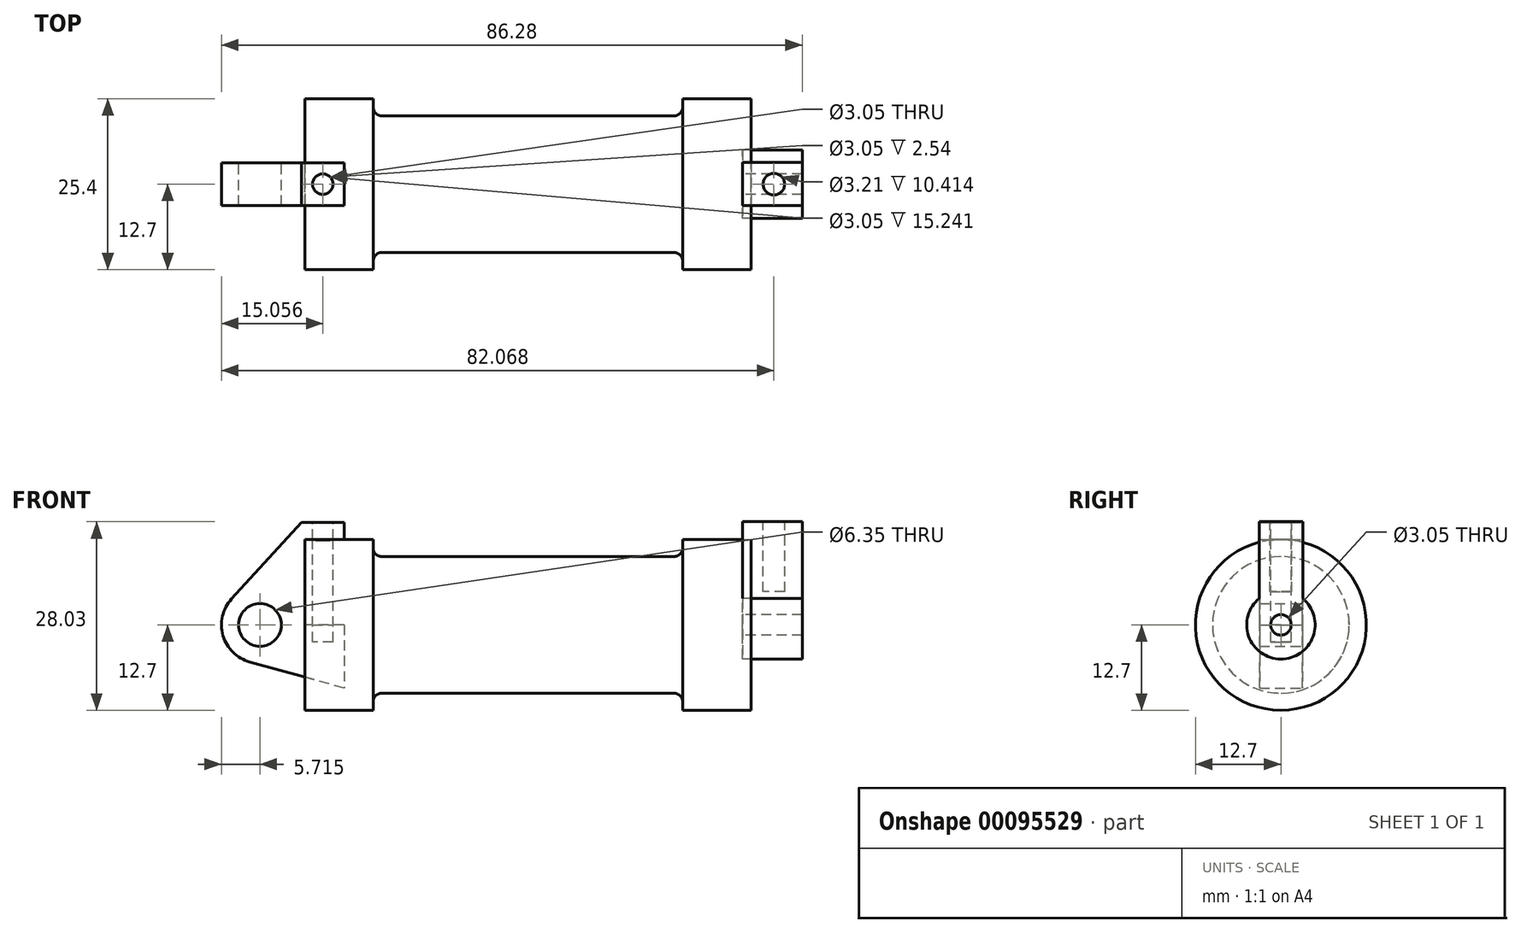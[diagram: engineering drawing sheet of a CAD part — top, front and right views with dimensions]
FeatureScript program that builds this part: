
annotation { "Feature Type Name" : "Feature", "Feature Type Description" : "" }
export const myFeature = defineFeature(function(context is Context, id is Id, definition is map)
    precondition{}
    {
        {
            var Q0;
            Q0=qCreatedBy(makeId("Front.planeOp"),FACE);
            var sketch = newSketch(context, id + "F0", { "sketchPlane" : qUnion([Q0])});
            skLineSegment(sketch, "E0", {"start": v(0, 0) * mm, "end": v(0, 12.7) * mm});
            skLineSegment(sketch, "E1", {"start": v(0, 12.7) * mm, "end": v(10.16, 12.7) * mm});
            skLineSegment(sketch, "E2", {"start": v(10.16, 12.7) * mm, "end": v(10.16, 10.16) * mm});
            skLineSegment(sketch, "E3", {"start": v(10.16, 10.16) * mm, "end": v(56.13, 10.16) * mm});
            skLineSegment(sketch, "E4", {"start": v(56.13, 10.16) * mm, "end": v(56.13, 12.7) * mm});
            skLineSegment(sketch, "E5", {"start": v(56.13, 12.7) * mm, "end": v(66.3, 12.7) * mm});
            skLineSegment(sketch, "E6", {"start": v(66.3, 12.7) * mm, "end": v(66.3, 0) * mm});
            skLineSegment(sketch, "E7", {"start": v(66.3, 0) * mm, "end": v(0, 0) * mm});
            skLineSegment(sketch, "E8", {"start": v(5.84, 15.24) * mm, "end": v(-0.5, 15.24) * mm});
            skLineSegment(sketch, "E9", {"start": v(-0.5, 15.24) * mm, "end": v(-10.88, 3.85) * mm});
            skLineSegment(sketch, "E10", {"start": v(0, 0) * mm, "end": v(-6.65, 0) * mm});
            skCircle(sketch, "E11", {"center": v(-6.65, 0) * mm, "radius": 5.72 * mm});
            skCircle(sketch, "E12", {"center": v(-6.65, 0) * mm, "radius": 3.18 * mm});
            skLineSegment(sketch, "E13", {"start": v(5.84, 15.24) * mm, "end": v(5.84, -9.4) * mm});
            skLineSegment(sketch, "E14", {"start": v(5.84, -9.4) * mm, "end": v(-8.18, -5.5) * mm});
            skSolve(sketch);
        }
        {
            var Q0;
            {var subQ0=sQuery(id+"F0.wireOp",EDGE,"E2");Q0=makeQuery(id+"F0.imprint","IMPRINT",FACE,{"disambiguationData":[TD([[makeQuery(id+"F0.imprint","IMPRINT",EDGE,{"derivedFrom":subQ0}),-1.0]])]});}
            var Q1;
            {var subQ0=sQuery(id+"F0.wireOp",EDGE,"E0");Q1=makeQuery(id+"F0.imprint","IMPRINT",FACE,{"disambiguationData":[TD([[makeQuery(id+"F0.imprint","IMPRINT",EDGE,{"derivedFrom":subQ0}),-1.0]])]});}
            var Q2;
            Q2=sQuery(id+"F0.wireOp",EDGE,"E7");
            revolve(context, id + "F1", {"entities" : qUnion([Q0, Q1]), "axis" : qUnion([Q2]), "revolveType" : RevolveType.FULL});
        }
        {
            var Q0;
            {var subQ3=sQuery(id+"F0.wireOp",EDGE,"E0");Q0=makeQuery(id+"F0.imprint","IMPRINT",FACE,{"disambiguationData":[TD([[makeQuery(id+"F0.imprint","IMPRINT",EDGE,{"derivedFrom":subQ3}),1.0]])]});}
            var Q1;
            {var subQ0=sQuery(id+"F0.wireOp",EDGE,"E14");Q1=makeQuery(id+"F0.imprint","IMPRINT",FACE,{"disambiguationData":[TD([[makeQuery(id+"F0.imprint","IMPRINT",EDGE,{"derivedFrom":subQ0}),-1.0]])]});}
            var Q2;
            {var subQ4=sQuery(id+"F0.wireOp",EDGE,"E12");Q2=makeQuery(id+"F0.imprint","IMPRINT",FACE,{"disambiguationData":[TD([[makeQuery(id+"F0.imprint","IMPRINT",EDGE,{"derivedFrom":subQ4}),-1.0]])]});}
            extrude(context, id + "F2", {"entities" : qUnion([Q0, Q1, Q2]), "endBound" : BoundingType.SYMMETRIC, "depth" : 6.35 * mm});
        }
        {
            var Q0;
            Q0=makeQuery(id+"F1.opRevolve","SWEPT_FACE",FACE,{"disambiguationData":[OSD([sQuery(id+"F0.wireOp",EDGE,"E6")])]});
            var sketch = newSketch(context, id + "F3", { "sketchPlane" : qUnion([Q0])});
            skCircle(sketch, "E15", {"center": v(0, 0) * mm, "radius": 1.52 * mm});
            skCircle(sketch, "E16", {"center": v(0, 0) * mm, "radius": 5.08 * mm});
            skLineSegment(sketch, "E17", {"start": v(-12.7, 0) * mm, "end": v(-12.7, 15.24) * mm});
            skLineSegment(sketch, "E18", {"start": v(12.7, 0) * mm, "end": v(12.7, 15.24) * mm});
            skLineSegment(sketch, "E19.bottom", {"start": v(-3.21, 15.33) * mm, "end": v(3.25, 15.33) * mm});
            skLineSegment(sketch, "E19.top", {"start": v(-3.21, 0) * mm, "end": v(3.25, 0) * mm});
            skLineSegment(sketch, "E19.left", {"start": v(-3.21, 15.33) * mm, "end": v(-3.21, 0) * mm});
            skLineSegment(sketch, "E19.right", {"start": v(3.25, 15.33) * mm, "end": v(3.25, 0) * mm});
            skSolve(sketch);
        }
        {
            var Q0;
            {var subQ0=sQuery(id+"F3.wireOp",EDGE,"E19.left");var subQ1=sQuery(id+"F3.wireOp",EDGE,"E16");var subQ2=makeQuery(id+"F3.imprint","INTERSECT",VERTEX,{"derivedFrom":[subQ1,subQ0]});Q0=makeQuery(id+"F3.imprint","IMPRINT",FACE,{"disambiguationData":[TD([[makeQuery(id+"F3.imprint","IMPRINT",EDGE,{"disambiguationData":[TD([[subQ2,1.0]])],"derivedFrom":subQ1}),-1.0]])]});}
            var Q1;
            {var subQ1=sQuery(id+"F3.wireOp",EDGE,"E19.top");var subQ3=sQuery(id+"F3.wireOp",EDGE,"E15");var subQ7=makeQuery(id+"F3.imprint","INTERSECT",VERTEX,{"disambiguationData":[OD(0.0)],"derivedFrom":[subQ3,subQ1]});Q1=makeQuery(id+"F3.imprint","IMPRINT",FACE,{"disambiguationData":[TD([[makeQuery(id+"F3.imprint","IMPRINT",EDGE,{"disambiguationData":[TD([[subQ7,-1.0]])],"derivedFrom":subQ3}),-1.0]])]});}
            var Q2;
            {var subQ1=sQuery(id+"F3.wireOp",EDGE,"E19.top");var subQ3=sQuery(id+"F3.wireOp",EDGE,"E15");var subQ7=makeQuery(id+"F3.imprint","INTERSECT",VERTEX,{"disambiguationData":[OD(0.0)],"derivedFrom":[subQ3,subQ1]});Q2=makeQuery(id+"F3.imprint","IMPRINT",FACE,{"disambiguationData":[TD([[makeQuery(id+"F3.imprint","IMPRINT",EDGE,{"disambiguationData":[TD([[subQ7,1.0]])],"derivedFrom":subQ3}),-1.0]])]});}
            var Q3;
            {var subQ0=sQuery(id+"F3.wireOp",EDGE,"E19.bottom");Q3=makeQuery(id+"F3.imprint","IMPRINT",FACE,{"disambiguationData":[TD([[makeQuery(id+"F3.imprint","IMPRINT",EDGE,{"derivedFrom":subQ0}),-1.0]])]});}
            extrude(context, id + "F4", {"entities" : qUnion([Q0, Q1, Q2, Q3]), "depth" : 7.62 * mm, "hasSecondDirection" : true, "secondDirectionOppositeDirection" : true, "secondDirectionDepth" : 1.27 * mm});
        }
        {
            var Q0;
            Q0=makeQuery(id+"F2.opExtrude","SWEPT_FACE",FACE,{"disambiguationData":[OSD([sQuery(id+"F0.wireOp",EDGE,"E8")])]});
            var sketch = newSketch(context, id + "F5", { "sketchPlane" : qUnion([Q0])});
            skCircle(sketch, "E20", {"center": v(2.69, 0) * mm, "radius": 1.52 * mm});
            skSolve(sketch);
        }
        {
            var Q0;
            Q0=makeQuery(id+"F5.imprint","IMPRINT",FACE,{"disambiguationData":[TD([[makeQuery(id+"F5.imprint","IMPRINT",EDGE,{"derivedFrom":sQuery(id+"F5.wireOp",EDGE,"E20")}),1.0]])]});
            extrude(context, id + "F6", {"entities" : qUnion([Q0]), "operationType" : NewBodyOperationType.REMOVE, "oppositeDirection" : true, "depth" : 17.78 * mm});
        }
        {
            var Q0;
            Q0=makeQuery(id+"F4.opExtrude","SWEPT_FACE",FACE,{"disambiguationData":[OSD([sQuery(id+"F3.wireOp",EDGE,"E19.bottom")])]});
            var sketch = newSketch(context, id + "F7", { "sketchPlane" : qUnion([Q0])});
            skCircle(sketch, "E21", {"center": v(69.7, 0) * mm, "radius": 1.6 * mm});
            skSolve(sketch);
        }
        {
            var Q0;
            Q0=makeQuery(id+"F7.imprint","IMPRINT",FACE,{"disambiguationData":[TD([[makeQuery(id+"F7.imprint","IMPRINT",EDGE,{"derivedFrom":sQuery(id+"F7.wireOp",EDGE,"E21")}),1.0]])]});
            extrude(context, id + "F8", {"entities" : qUnion([Q0]), "operationType" : NewBodyOperationType.REMOVE, "oppositeDirection" : true, "depth" : 10.4 * mm});
        }
        {
            var Q0;
            Q0=makeQuery(id+"F1.opRevolve","SWEPT_FACE",FACE,{"disambiguationData":[OSD([sQuery(id+"F0.wireOp",EDGE,"E3")])]});
            fillet(context, id + "F9", {"entities" : qUnion([Q0]), "radius" : 1.27 * mm, "tangentPropagation" : true, "allowEdgeOverflow" : false});
        }
    });
